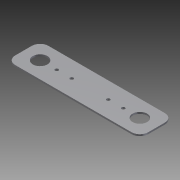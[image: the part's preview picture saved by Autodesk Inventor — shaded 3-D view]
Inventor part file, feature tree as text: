
AUTODESK INVENTOR PART (.ipt)
format: ipt  version: 2012 (Build 160160000, 160)  size: 96,768 bytes
history: native  units: mm
features: extrude x1, sketch x1
ambient origin geometry x8: Origin, YZ Plane, XZ Plane, XY Plane, X Axis, Y Axis, Z Axis, Center Point
bodies: Solid1 (feature_tree)
feature tree (2):
  extrude  "Extrusion1"  Depth=1.0mm TaperAngle=0.0deg
  sketch  "Sketch1"  dims[d109=10.0mm d110=10.0mm d111=8.77mm d112=8.77mm d113=2.0mm d114=2.0mm d115=10.0mm d116=9.0mm d117=2.0mm d118=2.0mm d119=10.0mm d120=9.0mm d121=60.0mm d126=10.0mm d399=1.0mm d400=0.0mm]
